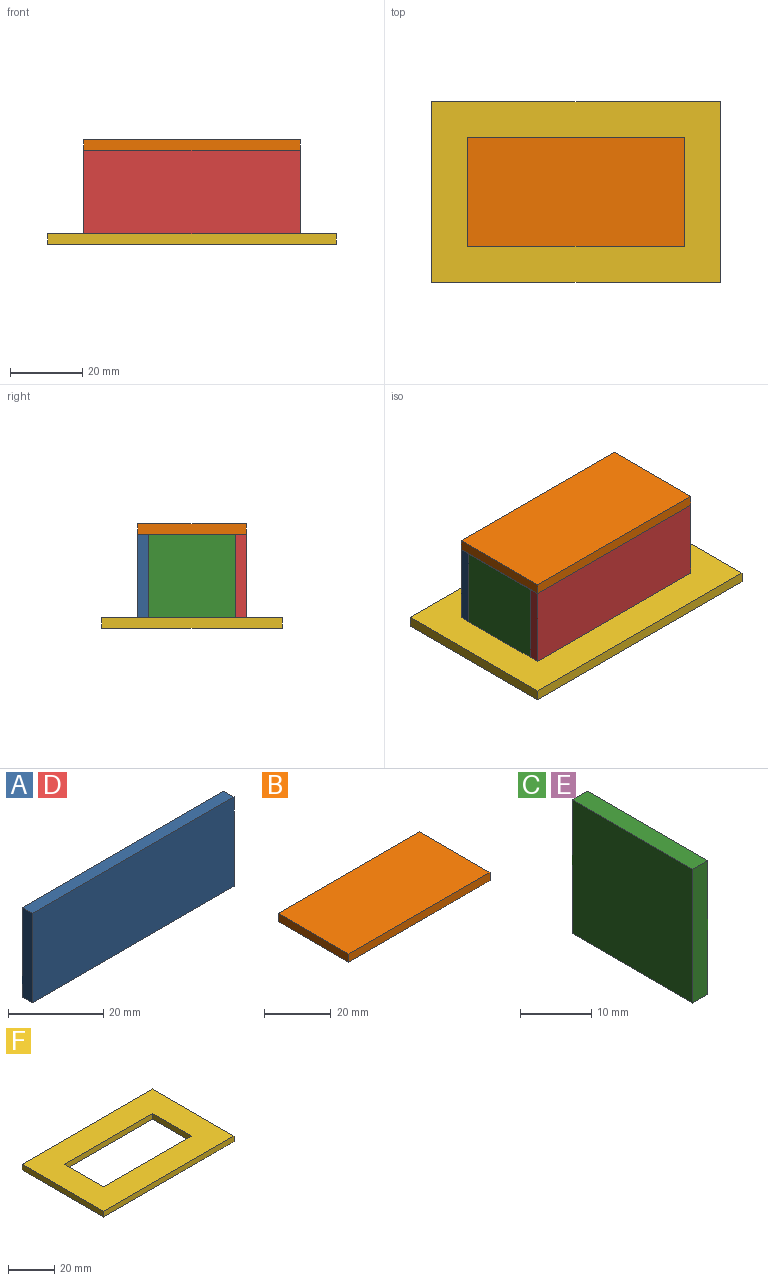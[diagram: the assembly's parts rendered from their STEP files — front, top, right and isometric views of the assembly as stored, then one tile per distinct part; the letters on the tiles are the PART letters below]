
ASSEMBLY  parts=6 mates=5
PART A: 6 faces, bbox 60x3x23 mm
  f0: plane 23x3mm, normal (1,0,0), area 69mm2, adj f1,f3,f4,f5
  f1: plane 60x3mm, normal (0,0,-1), area 180mm2, adj f0,f2,f4,f5
  f2: plane 23x3mm, normal (-1,0,0), area 69mm2, adj f1,f3,f4,f5
  f3: plane 60x3mm, normal (0,0,1), area 180mm2, adj f0,f2,f4,f5
  f4: plane 60x23mm, normal (0,1,0), area 1380mm2, adj f0,f1,f2,f3
  f5: plane 60x23mm, normal (0,-1,0), area 1380mm2, adj f0,f1,f2,f3
PART B: 6 faces, bbox 60x30x3 mm
  f0: plane 30x3mm, normal (1,0,0), area 90mm2, adj f1,f3,f4,f5
  f1: plane 60x3mm, normal (0,-1,0), area 180mm2, adj f0,f2,f4,f5
  f2: plane 30x3mm, normal (-1,0,0), area 90mm2, adj f1,f3,f4,f5
  f3: plane 60x3mm, normal (0,1,0), area 180mm2, adj f0,f2,f4,f5
  f4: plane 60x30mm, normal (0,0,-1), area 1800mm2, adj f0,f1,f2,f3
  f5: plane 60x30mm, normal (0,0,1), area 1800mm2, adj f0,f1,f2,f3
PART C: 6 faces, bbox 3x24x23 mm
  f0: plane 23x3mm, normal (0,1,0), area 69mm2, adj f1,f3,f4,f5
  f1: plane 24x3mm, normal (0,0,-1), area 72mm2, adj f0,f2,f4,f5
  f2: plane 23x3mm, normal (0,-1,0), area 69mm2, adj f1,f3,f4,f5
  f3: plane 24x3mm, normal (0,0,1), area 72mm2, adj f0,f2,f4,f5
  f4: plane 24x23mm, normal (-1,0,0), area 552mm2, adj f0,f1,f2,f3
  f5: plane 24x23mm, normal (1,0,0), area 552mm2, adj f0,f1,f2,f3
PART D: same geometry as A
PART E: same geometry as C
PART F: 10 faces, bbox 80x50x3 mm
  f0: plane 54x3mm, normal (0,-1,0), area 162mm2, adj f1,f7,f8,f9
  f1: plane 24x3mm, normal (1,0,0), area 72mm2, adj f0,f2,f8,f9
  f2: plane 54x3mm, normal (0,1,0), area 162mm2, adj f1,f7,f8,f9
  f3: plane 50x3mm, normal (1,0,0), area 150mm2, adj f4,f6,f8,f9
  f4: plane 80x3mm, normal (0,-1,0), area 240mm2, adj f3,f5,f8,f9
  f5: plane 50x3mm, normal (-1,0,0), area 150mm2, adj f4,f6,f8,f9
  f6: plane 80x3mm, normal (0,1,0), area 240mm2, adj f3,f5,f8,f9
  f7: plane 24x3mm, normal (-1,0,0), area 72mm2, adj f0,f2,f8,f9
  f8: plane 80x50mm, normal (0,0,-1), area 2704mm2, adj f0,f1,f2,f3,f4,f5,f6,f7
  f9: plane 80x50mm, normal (0,0,1), area 2704mm2, adj f0,f1,f2,f3,f4,f5,f6,f7
PLACE A t=(-27.26,-15,-38.63)mm
PLACE B t=(-27.26,-45,-15.63)mm
PLACE C t=(-27.26,-42,-38.63)mm
PLACE D t=(-27.26,-42,-38.63)mm
PLACE E t=(29.74,-42,-38.63)mm
PLACE F t=(-24.26,-42,-41.63)mm
MATE fastened C.f3 <-> B.f4  axis (0,0,1) through (-27.26,-30,-15.63)mm
MATE fastened B.f4 <-> A.f3  axis (0,0,-1) through (2.74,-15,-15.63)mm
MATE fastened C.f1 <-> F.f9  axis (0,0,-1) through (-24.26,-30,-38.63)mm
MATE fastened D.f3 <-> B.f4  axis (0,0,1) through (2.74,-45,-15.63)mm
MATE fastened B.f4 <-> E.f3  axis (0,0,-1) through (32.74,-30,-15.63)mm
